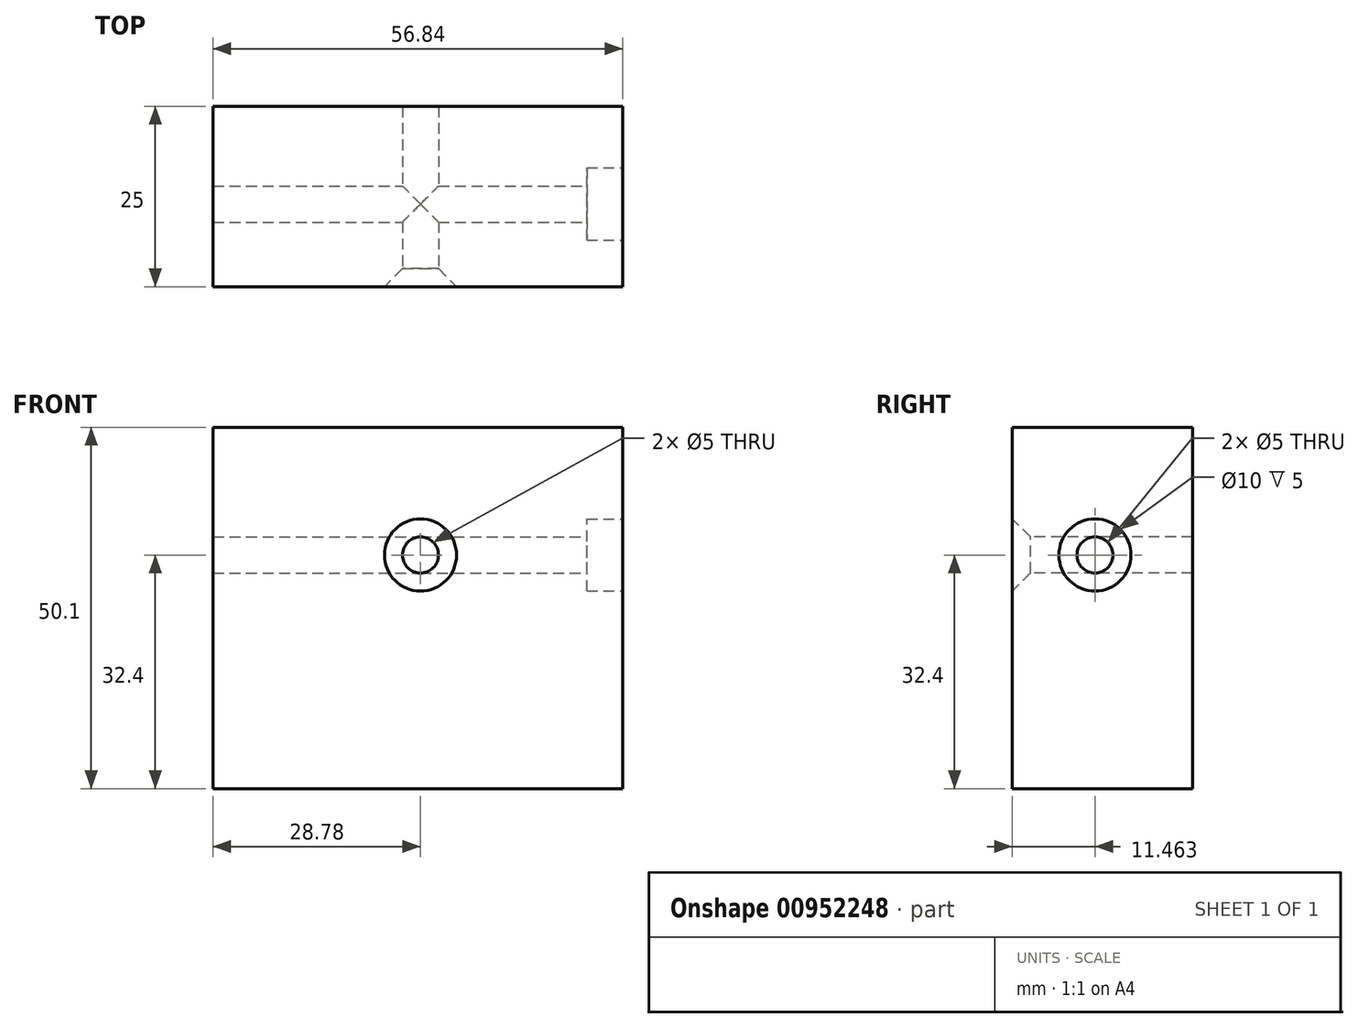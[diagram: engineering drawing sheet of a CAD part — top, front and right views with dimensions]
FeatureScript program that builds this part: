
annotation { "Feature Type Name" : "Feature", "Feature Type Description" : "" }
export const myFeature = defineFeature(function(context is Context, id is Id, definition is map)
    precondition{}
    {
        {
            var Q0;
            Q0=qCreatedBy(makeId("Front.planeOp"),FACE);
            var sketch = newSketch(context, id + "F0", { "sketchPlane" : qUnion([Q0])});
            skLineSegment(sketch, "E0.bottom", {"start": v(44.18, 17.7) * mm, "end": v(101.02, 17.7) * mm});
            skLineSegment(sketch, "E0.top", {"start": v(44.18, -32.4) * mm, "end": v(101.02, -32.4) * mm});
            skLineSegment(sketch, "E0.left", {"start": v(44.18, 17.7) * mm, "end": v(44.18, -32.4) * mm});
            skLineSegment(sketch, "E0.right", {"start": v(101.02, 17.7) * mm, "end": v(101.02, -32.4) * mm});
            skSolve(sketch);
        }
        {
            var Q0;
            Q0 = qSketchRegion(id + "F0", true);
            extrude(context, id + "F1", {"entities" : qUnion([Q0]), "depth" : 25 * mm, "offsetDistance" : 25 * mm});
        }
        {
            var Q0;
            Q0=makeQuery(id+"F1.opExtrude","CAP_FACE",FACE,{"disambiguationData":[OSD([sQuery(id+"F0.wireOp",EDGE,"E0.bottom"),sQuery(id+"F0.wireOp",EDGE,"E0.top"),sQuery(id+"F0.wireOp",EDGE,"E0.left"),sQuery(id+"F0.wireOp",EDGE,"E0.right")])],"isStart":false});
            var sketch = newSketch(context, id + "F2", { "sketchPlane" : qUnion([Q0])});
            skPoint(sketch, "E1", {"position": v(72.96, 0) * mm});
            skSolve(sketch);
        }
        {
            var Q0;
            Q0=sQuery(id+"F2.wireOp",VERTEX,"E1");
            var Q1;
            Q1=makeQuery(id+"F1.opExtrude","SWEPT_BODY",BODY,{"disambiguationData":[OSD([sQuery(id+"F0.wireOp",EDGE,"E0.bottom"),sQuery(id+"F0.wireOp",EDGE,"E0.top"),sQuery(id+"F0.wireOp",EDGE,"E0.left"),sQuery(id+"F0.wireOp",EDGE,"E0.right")])]});
            hole(context, id + "F3", {"style" : HoleStyle.C_SINK, "endStyle" : HoleEndStyle.THROUGH, "holeDiameter" : 5 * mm, "cSinkDiameter" : 10 * mm, "cSinkAngle" : 90 * degree, "majorDiameter" : 5 * mm, "isTappedThrough" : true, "tappedDepth" : 12 * mm, "tapClearance" : 3, "locations" : qUnion([Q0]), "scope" : qUnion([Q1])});
        }
        {
            var Q0;
            Q0=makeQuery(id+"F1.opExtrude","SWEPT_FACE",FACE,{"disambiguationData":[OSD([sQuery(id+"F0.wireOp",EDGE,"E0.right")])]});
            var sketch = newSketch(context, id + "F4", { "sketchPlane" : qUnion([Q0])});
            skPoint(sketch, "E2", {"position": v(-13.54, 0) * mm});
            skSolve(sketch);
        }
        {
            var Q0;
            Q0=sQuery(id+"F4.wireOp",VERTEX,"E2");
            var Q1;
            Q1=makeQuery(id+"F1.opExtrude","SWEPT_BODY",BODY,{"disambiguationData":[OSD([sQuery(id+"F0.wireOp",EDGE,"E0.bottom"),sQuery(id+"F0.wireOp",EDGE,"E0.top"),sQuery(id+"F0.wireOp",EDGE,"E0.left"),sQuery(id+"F0.wireOp",EDGE,"E0.right")])]});
            hole(context, id + "F5", {"style" : HoleStyle.C_SINK, "endStyle" : HoleEndStyle.THROUGH, "holeDiameter" : 5 * mm, "cSinkDiameter" : 10 * mm, "cSinkAngle" : 90 * degree, "majorDiameter" : 5 * mm, "isTappedThrough" : true, "tappedDepth" : 12 * mm, "tapClearance" : 3, "locations" : qUnion([Q0]), "scope" : qUnion([Q1])});
        }
        {
            var Q0;
            Q0=sQuery(id+"F4.wireOp",VERTEX,"E2");
            var Q1;
            Q1=makeQuery(id+"F1.opExtrude","SWEPT_BODY",BODY,{"disambiguationData":[OSD([sQuery(id+"F0.wireOp",EDGE,"E0.bottom"),sQuery(id+"F0.wireOp",EDGE,"E0.top"),sQuery(id+"F0.wireOp",EDGE,"E0.left"),sQuery(id+"F0.wireOp",EDGE,"E0.right")])]});
            hole(context, id + "F6", {"style" : HoleStyle.C_BORE, "endStyle" : HoleEndStyle.THROUGH, "holeDiameter" : 5 * mm, "cBoreDiameter" : 10 * mm, "cBoreDepth" : 5 * mm, "majorDiameter" : 5 * mm, "isTappedThrough" : true, "tappedDepth" : 12 * mm, "tapClearance" : 3, "locations" : qUnion([Q0]), "scope" : qUnion([Q1])});
        }
    });
